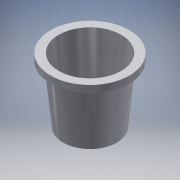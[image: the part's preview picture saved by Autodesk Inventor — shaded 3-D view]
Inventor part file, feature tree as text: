
AUTODESK INVENTOR PART (.ipt)
format: ipt  version: 2018 (Build 220112000, 112)  size: 232,960 bytes
history: native  units: in
note: dims shown in document units (in); Inventor stores cm internally (conversion verified against a paired STEP export)
features: sketch x2, revolve x1, extrude x1
ambient origin geometry x8: Origin, YZ Plane, XZ Plane, XY Plane, X Axis, Y Axis, Z Axis, Center Point
bodies: Solid1 (feature_tree)
feature tree (4):
  revolve  "Revolution1"  [1 undecoded]
  extrude  "Extrusion1"  Depth=0.1in
  sketch  "Sketch1"  dims[d0=0.07in d1=0.25in]
  sketch  "Sketch2"  dims[d2=0.1in d3=0.35in d4=0.07in d5=0.07in d6=0.1in d7=0.1in d9=0.1in d10=0.1in d11=0.0996in d12=0.6575in d13=0.6575in d14=90.0deg d15=0.2in d16=1.5748in d18=0.3in d19=1.5748in d21=0.3in d24=3.1496in d26=360.0deg d28=1.9375in d29=0.0in]
note: 1 required parameter value undecoded (feature->parameter linkage not recoverable at this tier; creation-order binding heuristic only, values carry confidence <= 0.55)
